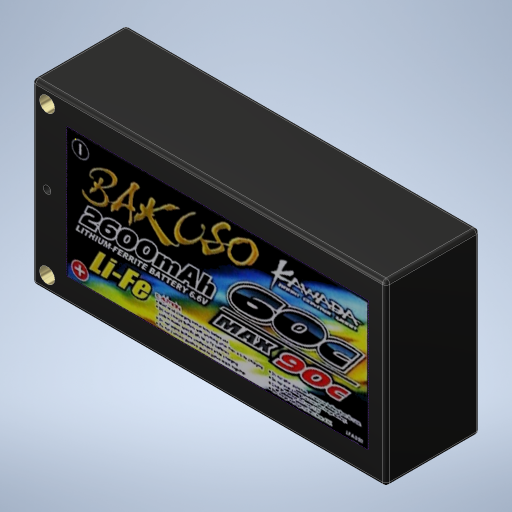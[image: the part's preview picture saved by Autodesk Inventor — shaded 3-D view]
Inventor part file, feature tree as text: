
AUTODESK INVENTOR PART (.ipt)
format: ipt  version: 2023.1 (Build 271208000, 208)  size: 451,584 bytes
history: native  units: mm
features: sketch x3, other x2, extrude x2, fillet x1, projected_geometry x1
ambient origin geometry x8: Origin, YZ Plane, XZ Plane, XY Plane, X Axis, Y Axis, Z Axis, Center Point
bodies: Body1 (feature_tree)
feature tree (9):
  other  "ソリッド1"
  extrude  "押し出し1"  Depth=93.0mm
  fillet  "フィレット1"  Radius=46.9mm
  sketch  "スケッチ2"
  extrude  "押し出し2"  Depth=24.7mm TaperAngle=0.0deg
  sketch  "スケッチ3"
  sketch  "スケッチ1"
  projected_geometry  "投影ループ1"
  other  "イメージ1"
